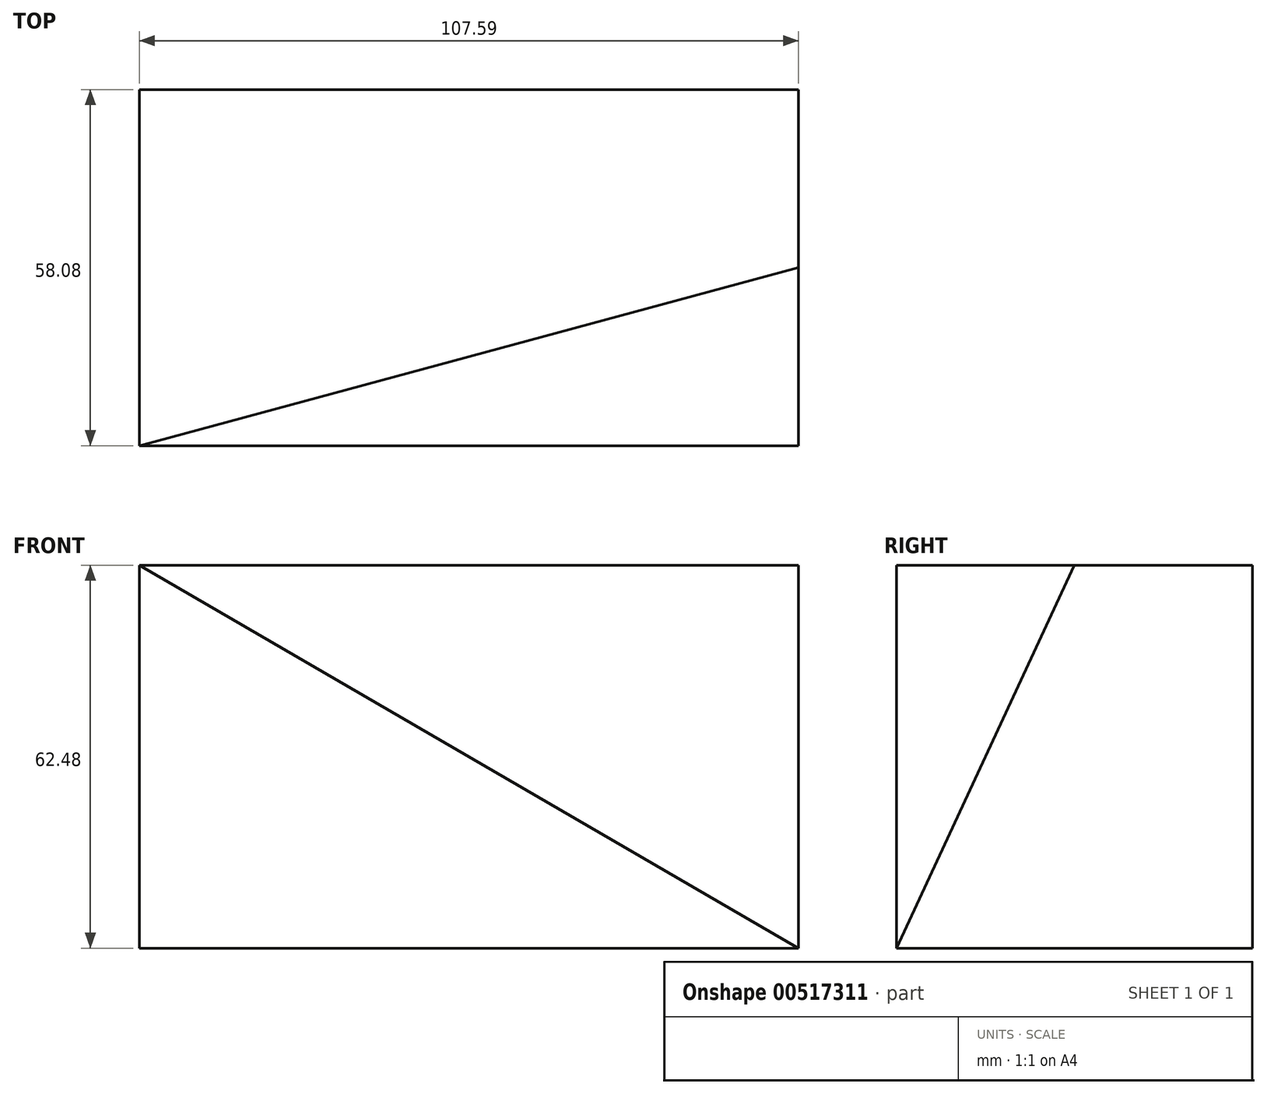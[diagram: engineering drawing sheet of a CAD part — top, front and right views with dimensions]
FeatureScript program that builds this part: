
annotation { "Feature Type Name" : "Feature", "Feature Type Description" : "" }
export const myFeature = defineFeature(function(context is Context, id is Id, definition is map)
    precondition{}
    {
        {
            var Q0;
            Q0=qCreatedBy(makeId("Top.planeOp"),FACE);
            var sketch = newSketch(context, id + "F0", { "sketchPlane" : qUnion([Q0])});
            skLineSegment(sketch, "E0.bottom", {"start": v(-76.88, -7.71) * mm, "end": v(30.71, -7.71) * mm});
            skLineSegment(sketch, "E0.top", {"start": v(-76.88, -65.8) * mm, "end": v(30.71, -65.8) * mm});
            skLineSegment(sketch, "E0.left", {"start": v(-76.88, -7.71) * mm, "end": v(-76.88, -65.8) * mm});
            skLineSegment(sketch, "E0.right", {"start": v(30.71, -7.71) * mm, "end": v(30.71, -65.8) * mm});
            skSolve(sketch);
        }
        {
            var Q0;
            Q0 = qSketchRegion(id + "F0", true);
            extrude(context, id + "F1", {"entities" : qUnion([Q0]), "depth" : 62.48 * mm, "offsetDistance" : 25.4 * mm});
        }
        {
            var Q0;
            Q0=makeQuery(id+"F1.opExtrude","CAP_EDGE",EDGE,{"disambiguationData":[OSD([sQuery(id+"F0.wireOp",EDGE,"E0.right")])],"isStart":false});
            cPoint(context, id + "F2", {"entities" : qUnion([Q0]), "parameter" : 0.5});
        }
        {
            var Q0;
            Q0=makeQuery(id+"F1.opExtrude","CAP_VERTEX",VERTEX,{"disambiguationData":[OSD([sQuery(id+"F0.wireOp",EDGE,"E0.top"),sQuery(id+"F0.wireOp",EDGE,"E0.left")])],"isStart":false});
            var Q1;
            Q1=makeQuery(id+"F1.opExtrude","CAP_VERTEX",VERTEX,{"disambiguationData":[OSD([sQuery(id+"F0.wireOp",EDGE,"E0.top"),sQuery(id+"F0.wireOp",EDGE,"E0.right")])],"isStart":true});
            var Q2;
            Q2 = qCreatedBy(id + "F2" ,VERTEX);
            cPlane(context, id + "F3", {"entities" : qUnion([Q0, Q1, Q2]), "cplaneType" : CPlaneType.THREE_POINT, "offset" : 25.4 * mm, "width" : 152.4 * mm, "height" : 152.4 * mm});
        }
        {
            var Q0;
            Q0=qCreatedBy(id+"F3.planeOp",FACE);
            var sketch = newSketch(context, id + "F4", { "sketchPlane" : qUnion([Q0])});
            skLineSegment(sketch, "E1", {"start": v(95.12, 28.93) * mm, "end": v(-15.65, 41.17) * mm});
            skLineSegment(sketch, "E2", {"start": v(95.12, 28.93) * mm, "end": v(-15.65, -27.73) * mm});
            skLineSegment(sketch, "E3", {"start": v(-15.65, 41.17) * mm, "end": v(-15.65, -27.73) * mm});
            skSolve(sketch);
        }
        {
            var Q0;
            Q0 = qSketchRegion(id + "F4", true);
            extrude(context, id + "F5", {"entities" : qUnion([Q0]), "operationType" : NewBodyOperationType.REMOVE, "endBound" : BoundingType.THROUGH_ALL, "oppositeDirection" : true, "depth" : 25.4 * mm, "offsetDistance" : 25.4 * mm});
        }
    });
